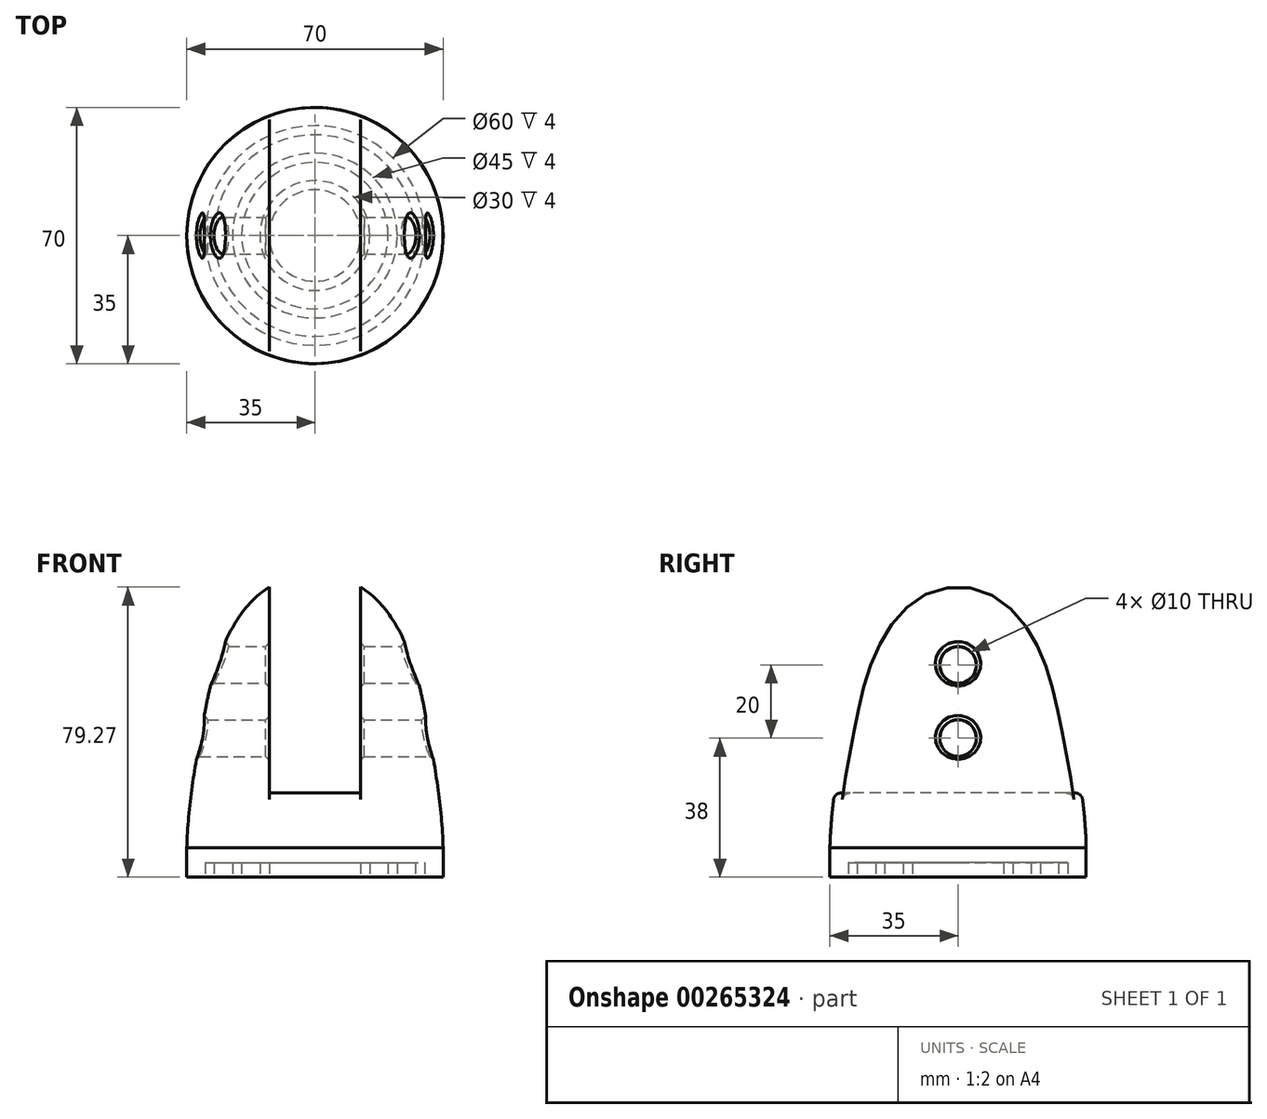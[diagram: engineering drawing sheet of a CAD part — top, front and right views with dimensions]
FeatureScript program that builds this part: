
annotation { "Feature Type Name" : "Feature", "Feature Type Description" : "" }
export const myFeature = defineFeature(function(context is Context, id is Id, definition is map)
    precondition{}
    {
        {
            var Q0;
            Q0=qCreatedBy(makeId("Front.planeOp"),FACE);
            var sketch = newSketch(context, id + "F0", { "sketchPlane" : qUnion([Q0])});
            skLineSegment(sketch, "E0", {"start": v(0, 0) * mm, "end": v(0, 200) * mm, "construction": true});
            skLineSegment(sketch, "E1", {"start": v(0, 0) * mm, "end": v(35, 0) * mm});
            skFitSpline(sketch, "E2", {"points": [v(35, 0) * mm, v(31.03, 31.72) * mm, v(26.44, 51.41) * mm, v(16.56, 68.1) * mm, v(0, 75) * mm], "startDerivative": vector(-2.55, 113.57) * mm, "endDerivative": vector(-90.73, 5.07) * mm});
            skLineSegment(sketch, "E3", {"start": v(0, 75) * mm, "end": v(0, 0) * mm});
            skSolve(sketch);
        }
        {
            var Q0;
            Q0=makeQuery(id+"F0.imprint","IMPRINT",FACE,{"disambiguationData":[TD([[makeQuery(id+"F0.imprint","IMPRINT",EDGE,{"derivedFrom":sQuery(id+"F0.wireOp",EDGE,"E1")}),1.0]])]});
            var Q1;
            Q1=sQuery(id+"F0.wireOp",EDGE,"E0");
            revolve(context, id + "F1", {"entities" : qUnion([Q0]), "axis" : qUnion([Q1]), "revolveType" : RevolveType.FULL});
        }
        {
            var Q0;
            Q0=makeQuery(id+"F1.opRevolve","SWEPT_FACE",FACE,{"disambiguationData":[OSD([sQuery(id+"F0.wireOp",EDGE,"E1")])]});
            extrude(context, id + "F2", {"entities" : qUnion([Q0]), "depth" : 8 * mm});
        }
        {
            var Q0;
            Q0=qCreatedBy(makeId("Front.planeOp"),FACE);
            var sketch = newSketch(context, id + "F3", { "sketchPlane" : qUnion([Q0])});
            skLineSegment(sketch, "E4", {"start": v(0, 0) * mm, "end": v(0, 100) * mm, "construction": true});
            skLineSegment(sketch, "E5.bottom", {"start": v(-12.5, 15) * mm, "end": v(12.5, 15) * mm});
            skLineSegment(sketch, "E5.top", {"start": v(-12.5, 85) * mm, "end": v(12.5, 85) * mm});
            skLineSegment(sketch, "E5.left", {"start": v(-12.5, 15) * mm, "end": v(-12.5, 85) * mm});
            skLineSegment(sketch, "E5.right", {"start": v(12.5, 15) * mm, "end": v(12.5, 85) * mm});
            skSolve(sketch);
        }
        {
            var Q0;
            Q0=makeQuery(id+"F3.imprint","IMPRINT",FACE,{"disambiguationData":[TD([[makeQuery(id+"F3.imprint","IMPRINT",EDGE,{"derivedFrom":sQuery(id+"F3.wireOp",EDGE,"E5.bottom")}),1.0]])]});
            extrude(context, id + "F4", {"entities" : qUnion([Q0]), "operationType" : NewBodyOperationType.REMOVE, "endBound" : BoundingType.SYMMETRIC, "oppositeDirection" : true, "depth" : 100 * mm});
        }
        {
            var Q0;
            Q0=makeQuery(id+"F4.boolean.opBoolean","INTERSECT",EDGE,{"disambiguationData":[OD(1.0)],"derivedFrom":[makeQuery(id+"F1.opRevolve","SWEPT_FACE",FACE,{"disambiguationData":[OSD([sQuery(id+"F0.wireOp",EDGE,"E2")])]}),makeQuery(id+"F4.opExtrude","SWEPT_FACE",FACE,{"disambiguationData":[OSD([sQuery(id+"F3.wireOp",EDGE,"E5.bottom")])]})]});
            var Q1;
            Q1=makeQuery(id+"F4.boolean.opBoolean","INTERSECT",EDGE,{"disambiguationData":[OD(0.0)],"derivedFrom":[makeQuery(id+"F1.opRevolve","SWEPT_FACE",FACE,{"disambiguationData":[OSD([sQuery(id+"F0.wireOp",EDGE,"E2")])]}),makeQuery(id+"F4.opExtrude","SWEPT_FACE",FACE,{"disambiguationData":[OSD([sQuery(id+"F3.wireOp",EDGE,"E5.bottom")])]})]});
            fillet(context, id + "F5", {"entities" : qUnion([Q0, Q1]), "radius" : 2 * mm, "tangentPropagation" : true, "allowEdgeOverflow" : false});
        }
        {
            var Q0;
            Q0=qCreatedBy(makeId("Right.planeOp"),FACE);
            var sketch = newSketch(context, id + "F6", { "sketchPlane" : qUnion([Q0])});
            skLineSegment(sketch, "E6", {"start": v(-61.32, 50) * mm, "end": v(127.85, 50) * mm, "construction": true});
            skLineSegment(sketch, "E7.0", {"start": v(-61.32, 30) * mm, "end": v(127.85, 30) * mm, "construction": true});
            skLineSegment(sketch, "E8", {"start": v(0, 0) * mm, "end": v(0, 101.95) * mm, "construction": true});
            skCircle(sketch, "E9", {"center": v(0, 30) * mm, "radius": 5 * mm});
            skCircle(sketch, "E10", {"center": v(0, 50) * mm, "radius": 5 * mm});
            skSolve(sketch);
        }
        {
            var Q0;
            Q0=makeQuery(id+"F6.imprint","IMPRINT",FACE,{"disambiguationData":[TD([[makeQuery(id+"F6.imprint","IMPRINT",EDGE,{"derivedFrom":sQuery(id+"F6.wireOp",EDGE,"E10")}),1.0]])]});
            var Q1;
            Q1=makeQuery(id+"F6.imprint","IMPRINT",FACE,{"disambiguationData":[TD([[makeQuery(id+"F6.imprint","IMPRINT",EDGE,{"derivedFrom":sQuery(id+"F6.wireOp",EDGE,"E9")}),1.0]])]});
            extrude(context, id + "F7", {"entities" : qUnion([Q0, Q1]), "operationType" : NewBodyOperationType.REMOVE, "endBound" : BoundingType.SYMMETRIC, "oppositeDirection" : true, "depth" : 100 * mm});
        }
        {
            var Q0;
            Q0=makeQuery(id+"F7.boolean.opBoolean","INTERSECT",EDGE,{"disambiguationData":[OD(1.0)],"derivedFrom":[makeQuery(id+"F1.opRevolve","SWEPT_FACE",FACE,{"disambiguationData":[OSD([sQuery(id+"F0.wireOp",EDGE,"E2")])]}),makeQuery(id+"F7.opExtrude","SWEPT_FACE",FACE,{"disambiguationData":[OSD([sQuery(id+"F6.wireOp",EDGE,"E10")])]})]});
            var Q1;
            Q1=makeQuery(id+"F7.boolean.opBoolean","INTERSECT",EDGE,{"disambiguationData":[OD(1.0)],"derivedFrom":[makeQuery(id+"F1.opRevolve","SWEPT_FACE",FACE,{"disambiguationData":[OSD([sQuery(id+"F0.wireOp",EDGE,"E2")])]}),makeQuery(id+"F7.opExtrude","SWEPT_FACE",FACE,{"disambiguationData":[OSD([sQuery(id+"F6.wireOp",EDGE,"E9")])]})]});
            var Q2;
            Q2=makeQuery(id+"F7.boolean.opBoolean","INTERSECT",EDGE,{"derivedFrom":[makeQuery(id+"F4.boolean.opBoolean","COPY",FACE,{"derivedFrom":makeQuery(id+"F4.opExtrude","SWEPT_FACE",FACE,{"disambiguationData":[OSD([sQuery(id+"F3.wireOp",EDGE,"E5.right")])]})}),makeQuery(id+"F7.opExtrude","SWEPT_FACE",FACE,{"disambiguationData":[OSD([sQuery(id+"F6.wireOp",EDGE,"E10")])]})]});
            var Q3;
            Q3=makeQuery(id+"F7.boolean.opBoolean","INTERSECT",EDGE,{"derivedFrom":[makeQuery(id+"F4.boolean.opBoolean","COPY",FACE,{"derivedFrom":makeQuery(id+"F4.opExtrude","SWEPT_FACE",FACE,{"disambiguationData":[OSD([sQuery(id+"F3.wireOp",EDGE,"E5.right")])]})}),makeQuery(id+"F7.opExtrude","SWEPT_FACE",FACE,{"disambiguationData":[OSD([sQuery(id+"F6.wireOp",EDGE,"E9")])]})]});
            var Q4;
            Q4=makeQuery(id+"F7.boolean.opBoolean","INTERSECT",EDGE,{"disambiguationData":[OD(0.0)],"derivedFrom":[makeQuery(id+"F1.opRevolve","SWEPT_FACE",FACE,{"disambiguationData":[OSD([sQuery(id+"F0.wireOp",EDGE,"E2")])]}),makeQuery(id+"F7.opExtrude","SWEPT_FACE",FACE,{"disambiguationData":[OSD([sQuery(id+"F6.wireOp",EDGE,"E10")])]})]});
            var Q5;
            Q5=makeQuery(id+"F7.boolean.opBoolean","INTERSECT",EDGE,{"disambiguationData":[OD(0.0)],"derivedFrom":[makeQuery(id+"F1.opRevolve","SWEPT_FACE",FACE,{"disambiguationData":[OSD([sQuery(id+"F0.wireOp",EDGE,"E2")])]}),makeQuery(id+"F7.opExtrude","SWEPT_FACE",FACE,{"disambiguationData":[OSD([sQuery(id+"F6.wireOp",EDGE,"E9")])]})]});
            var Q6;
            Q6=makeQuery(id+"F7.boolean.opBoolean","INTERSECT",EDGE,{"derivedFrom":[makeQuery(id+"F4.boolean.opBoolean","COPY",FACE,{"derivedFrom":makeQuery(id+"F4.opExtrude","SWEPT_FACE",FACE,{"disambiguationData":[OSD([sQuery(id+"F3.wireOp",EDGE,"E5.left")])]})}),makeQuery(id+"F7.opExtrude","SWEPT_FACE",FACE,{"disambiguationData":[OSD([sQuery(id+"F6.wireOp",EDGE,"E9")])]})]});
            var Q7;
            Q7=makeQuery(id+"F7.boolean.opBoolean","INTERSECT",EDGE,{"derivedFrom":[makeQuery(id+"F4.boolean.opBoolean","COPY",FACE,{"derivedFrom":makeQuery(id+"F4.opExtrude","SWEPT_FACE",FACE,{"disambiguationData":[OSD([sQuery(id+"F3.wireOp",EDGE,"E5.left")])]})}),makeQuery(id+"F7.opExtrude","SWEPT_FACE",FACE,{"disambiguationData":[OSD([sQuery(id+"F6.wireOp",EDGE,"E10")])]})]});
            chamfer(context, id + "F8", {"entities" : qUnion([Q0, Q1, Q2, Q3, Q4, Q5, Q6, Q7]), "width" : 1 * mm, "tangentPropagation" : true});
        }
        {
            var Q0;
            Q0=makeQuery(id+"F2.opExtrude","CAP_FACE",FACE,{"disambiguationData":[OSD([sQuery(id+"F0.wireOp",EDGE,"E1")])],"isStart":false});
            var sketch = newSketch(context, id + "F9", { "sketchPlane" : qUnion([Q0])});
            skCircle(sketch, "E11", {"center": v(0, 0) * mm, "radius": 30 * mm});
            skCircle(sketch, "E12", {"center": v(0, 0) * mm, "radius": 27.5 * mm});
            skCircle(sketch, "E13", {"center": v(0, 0) * mm, "radius": 20 * mm});
            skCircle(sketch, "E14", {"center": v(0, 0) * mm, "radius": 22.5 * mm});
            skCircle(sketch, "E15", {"center": v(0, 0) * mm, "radius": 15 * mm});
            skCircle(sketch, "E16", {"center": v(0, 0) * mm, "radius": 12.5 * mm});
            skSolve(sketch);
        }
        {
            var Q0;
            Q0 = qSketchRegion(id + "F9", true);
            var Q1;
            Q1=makeQuery(id+"F9.imprint","IMPRINT",FACE,{"disambiguationData":[TD([[makeQuery(id+"F9.imprint","IMPRINT",EDGE,{"derivedFrom":sQuery(id+"F9.wireOp",EDGE,"E13")}),-1.0]])]});
            var Q2;
            Q2=makeQuery(id+"F9.imprint","IMPRINT",FACE,{"disambiguationData":[TD([[makeQuery(id+"F9.imprint","IMPRINT",EDGE,{"derivedFrom":sQuery(id+"F9.wireOp",EDGE,"E15")}),1.0]])]});
            extrude(context, id + "F10", {"entities" : qUnion([Q0, Q1, Q2]), "operationType" : NewBodyOperationType.REMOVE, "oppositeDirection" : true, "depth" : 4 * mm});
        }
    });
